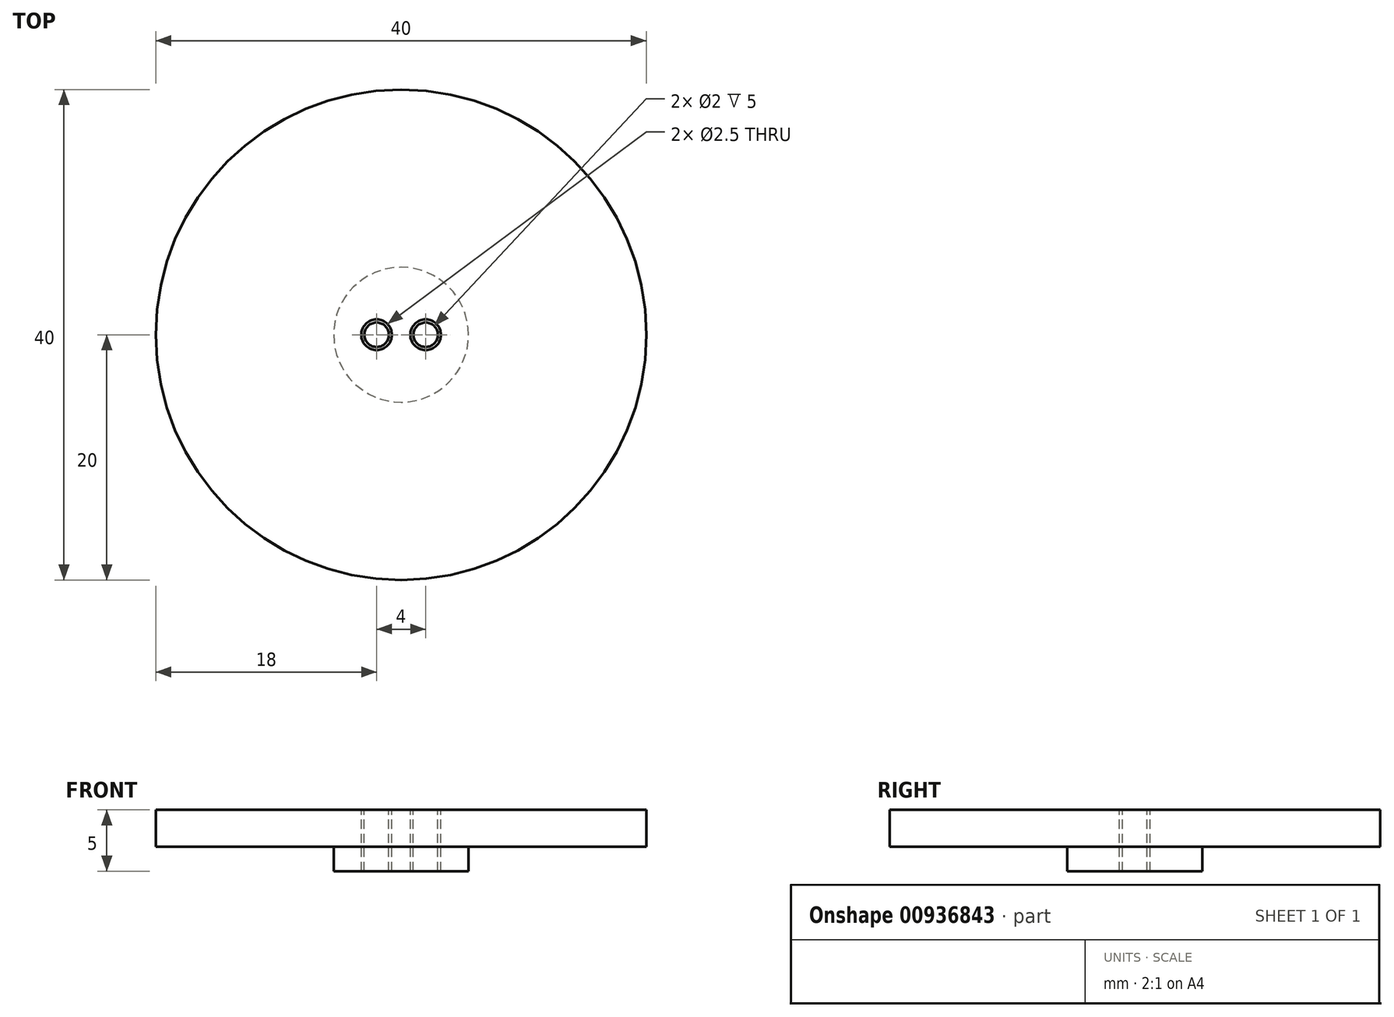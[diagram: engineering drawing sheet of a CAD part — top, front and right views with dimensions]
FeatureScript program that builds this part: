
annotation { "Feature Type Name" : "Feature", "Feature Type Description" : "" }
export const myFeature = defineFeature(function(context is Context, id is Id, definition is map)
    precondition{}
    {
        {
            var Q0;
            Q0=qCreatedBy(makeId("Top.planeOp"),FACE);
            var sketch = newSketch(context, id + "F0", { "sketchPlane" : qUnion([Q0])});
            skCircle(sketch, "E0", {"center": v(0, 0) * mm, "radius": 20 * mm});
            skSolve(sketch);
        }
        {
            var Q0;
            Q0 = qSketchRegion(id + "F0", true);
            extrude(context, id + "F1", {"entities" : qUnion([Q0]), "depth" : 3 * mm, "offsetDistance" : 25 * mm});
        }
        {
            var Q0;
            Q0=makeQuery(id+"F1.opExtrude","CAP_FACE",FACE,{"disambiguationData":[OSD([sQuery(id+"F0.wireOp",EDGE,"E0")])],"isStart":true});
            var sketch = newSketch(context, id + "F2", { "sketchPlane" : qUnion([Q0])});
            skCircle(sketch, "E1", {"center": v(0, 0) * mm, "radius": 5.5 * mm});
            skSolve(sketch);
        }
        {
            var Q0;
            Q0 = qSketchRegion(id + "F2", true);
            extrude(context, id + "F3", {"entities" : qUnion([Q0]), "operationType" : NewBodyOperationType.ADD, "depth" : 2 * mm, "offsetDistance" : 25 * mm});
        }
        {
            var Q0;
            Q0=makeQuery(id+"F1.opExtrude","CAP_FACE",FACE,{"disambiguationData":[OSD([sQuery(id+"F0.wireOp",EDGE,"E0")])],"isStart":false});
            var sketch = newSketch(context, id + "F4", { "sketchPlane" : qUnion([Q0])});
            skCircle(sketch, "E2", {"center": v(-2, 0) * mm, "radius": 1.25 * mm});
            skCircle(sketch, "E3", {"center": v(2, 0) * mm, "radius": 1.25 * mm});
            skSolve(sketch);
        }
        {
            var Q0;
            Q0 = qSketchRegion(id + "F4", true);
            extrude(context, id + "F5", {"entities" : qUnion([Q0]), "operationType" : NewBodyOperationType.REMOVE, "oppositeDirection" : true, "depth" : 25 * mm, "offsetDistance" : 25 * mm});
        }
        {
            var Q0;
            Q0=makeQuery(id+"F1.opExtrude","CAP_FACE",FACE,{"disambiguationData":[OSD([sQuery(id+"F0.wireOp",EDGE,"E0")])],"isStart":false});
            var sketch = newSketch(context, id + "F6", { "sketchPlane" : qUnion([Q0])});
            skCircle(sketch, "E4", {"center": v(-2, 0) * mm, "radius": 1.25 * mm});
            skCircle(sketch, "E5", {"center": v(2, 0) * mm, "radius": 1.25 * mm});
            skSolve(sketch);
        }
        {
            var Q0;
            Q0 = qSketchRegion(id + "F6", true);
            extrude(context, id + "F7", {"entities" : qUnion([Q0]), "oppositeDirection" : true, "depth" : 5 * mm, "offsetDistance" : 25 * mm});
        }
        {
            var Q0;
            Q0=makeQuery(id+"F1.opExtrude","CAP_FACE",FACE,{"disambiguationData":[OSD([sQuery(id+"F0.wireOp",EDGE,"E0")])],"isStart":false});
            var sketch = newSketch(context, id + "F8", { "sketchPlane" : qUnion([Q0])});
            skCircle(sketch, "E6", {"center": v(-2, 0) * mm, "radius": 1 * mm});
            skCircle(sketch, "E7", {"center": v(2, 0) * mm, "radius": 1 * mm});
            skSolve(sketch);
        }
        {
            var Q0;
            Q0 = qSketchRegion(id + "F8", true);
            extrude(context, id + "F9", {"entities" : qUnion([Q0]), "operationType" : NewBodyOperationType.REMOVE, "oppositeDirection" : true, "depth" : 25 * mm, "offsetDistance" : 25 * mm});
        }
    });
